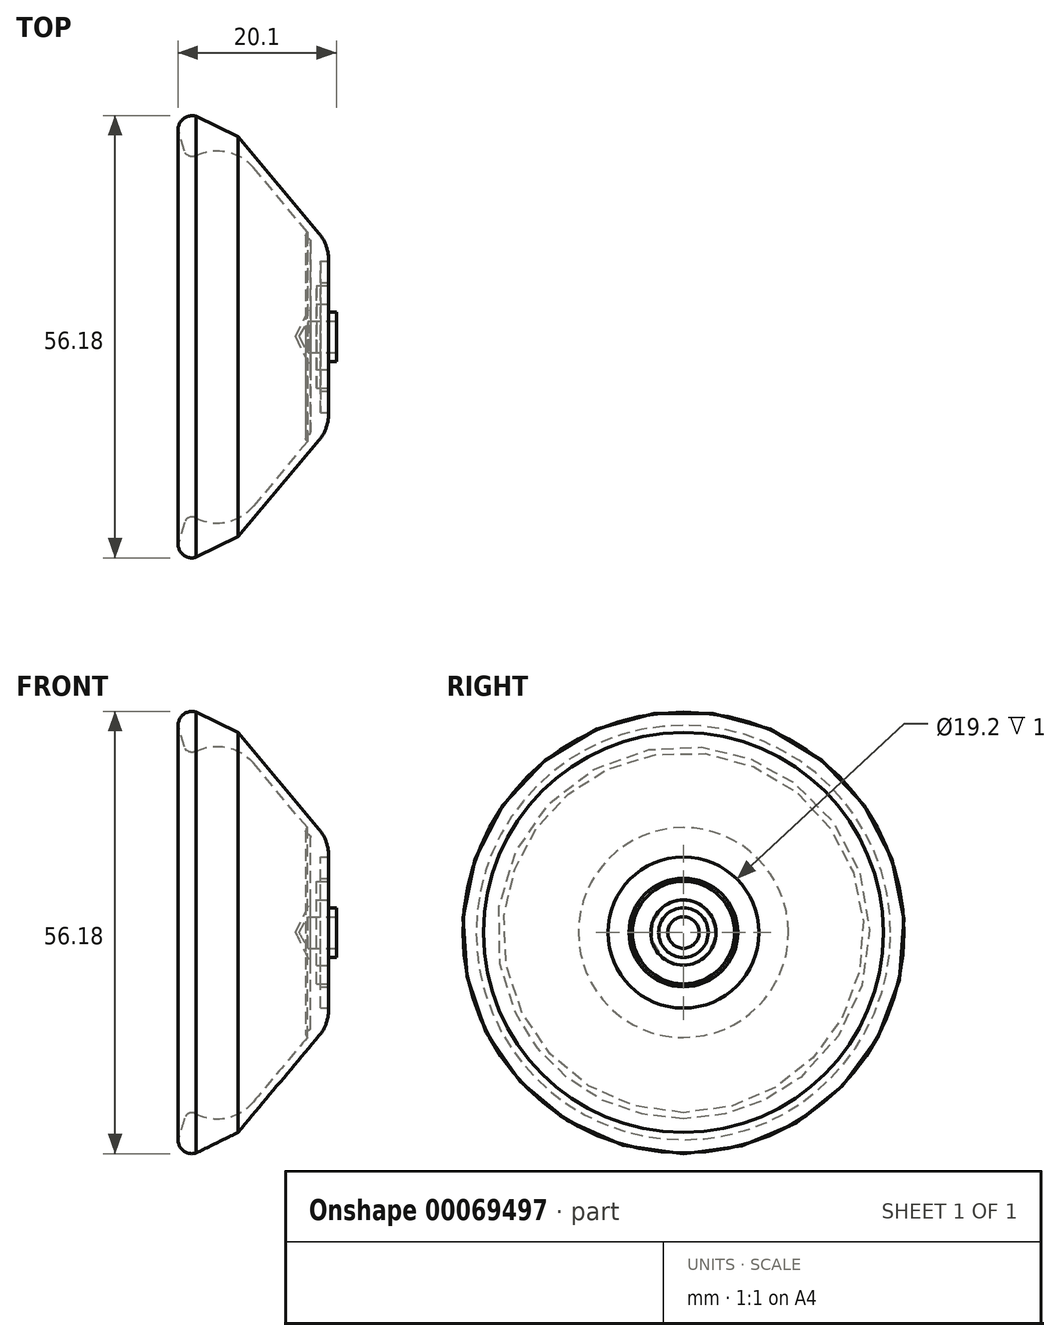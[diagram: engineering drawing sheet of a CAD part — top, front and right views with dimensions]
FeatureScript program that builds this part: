
annotation { "Feature Type Name" : "Feature", "Feature Type Description" : "" }
export const myFeature = defineFeature(function(context is Context, id is Id, definition is map)
    precondition{}
    {
        {
            var Q0;
            Q0=qCreatedBy(makeId("Front.planeOp"),FACE);
            var sketch = newSketch(context, id + "F0", { "sketchPlane" : qUnion([Q0])});
            skLineSegment(sketch, "E0", {"start": v(-1.4, 2) * mm, "end": v(-5, 2) * mm});
            skLineSegment(sketch, "E1", {"start": v(-5, 2) * mm, "end": v(-6.15, 0) * mm});
            skLineSegment(sketch, "E2", {"start": v(-6.15, 0) * mm, "end": v(-6.57, 0) * mm});
            skLineSegment(sketch, "E3", {"start": v(-5.08, 13.33) * mm, "end": v(-11.95, 21.51) * mm});
            skLineSegment(sketch, "E4", {"start": v(-1.4, 3.15) * mm, "end": v(-2.4, 3.15) * mm});
            skLineSegment(sketch, "E5", {"start": v(-2.4, 3.15) * mm, "end": v(-2.4, 4.15) * mm});
            skLineSegment(sketch, "E6", {"start": v(-2.4, 4.15) * mm, "end": v(-3.9, 4.15) * mm});
            skLineSegment(sketch, "E7", {"start": v(-3.9, 4.15) * mm, "end": v(-3.9, 6.5) * mm});
            skLineSegment(sketch, "E8", {"start": v(-3.9, 6.5) * mm, "end": v(-2.4, 6.5) * mm});
            skLineSegment(sketch, "E9", {"start": v(-2.4, 6.5) * mm, "end": v(-2.4, 6.9) * mm});
            skLineSegment(sketch, "E10", {"start": v(-2.4, 6.9) * mm, "end": v(-3.4, 6.9) * mm});
            skLineSegment(sketch, "E11", {"start": v(-3.4, 6.9) * mm, "end": v(-3.4, 9.6) * mm});
            skLineSegment(sketch, "E12", {"start": v(-3.4, 9.6) * mm, "end": v(-2.4, 9.6) * mm});
            skLineSegment(sketch, "E13", {"start": v(-2.4, 9.6) * mm, "end": v(-2.4, 9.87) * mm});
            skLineSegment(sketch, "E14", {"start": v(-1.4, 3.15) * mm, "end": v(-1.4, 2) * mm});
            skLineSegment(sketch, "E15", {"start": v(-13.9, 25.4) * mm, "end": v(-3.57, 13.09) * mm});
            skLineSegment(sketch, "E16", {"start": v(-4.65, 4) * mm, "end": v(-4.65, 12.1) * mm});
            skPoint(sketch, "E17.visualSharp", {"position": v(-2.4, 11.7) * mm});
            skArc(sketch, "E17.filletArc", {"start": v(-2.4, 9.87) * mm, "mid": v(-2.7, 11.58) * mm, "end": v(-3.57, 13.09) * mm});
            skLineSegment(sketch, "E18", {"start": v(-4.77, 12.34) * mm, "end": v(-5.12, 12.6) * mm});
            skLineSegment(sketch, "E19", {"start": v(-5.2, 13.16) * mm, "end": v(-5.08, 13.33) * mm});
            skPoint(sketch, "E20.visualSharp", {"position": v(-4.65, 12.25) * mm});
            skArc(sketch, "E20.filletArc", {"start": v(-4.65, 12.1) * mm, "mid": v(-4.68, 12.23) * mm, "end": v(-4.77, 12.34) * mm});
            skPoint(sketch, "E21.visualSharp", {"position": v(-5.44, 12.83) * mm});
            skArc(sketch, "E21.filletArc", {"start": v(-5.2, 13.16) * mm, "mid": v(-5.28, 12.86) * mm, "end": v(-5.12, 12.6) * mm});
            skLineSegment(sketch, "E22", {"start": v(-13.9, 25.4) * mm, "end": v(-19.2, 28) * mm});
            skArc(sketch, "E23", {"start": v(-19.2, 28) * mm, "mid": v(-20.78, 27.75) * mm, "end": v(-21.5, 26.32) * mm});
            skPoint(sketch, "E24.visualSharp", {"position": v(-15.03, 25.19) * mm});
            skArc(sketch, "E24.filletArc", {"start": v(-11.95, 21.51) * mm, "mid": v(-15.35, 23.54) * mm, "end": v(-19.27, 23) * mm});
            skLineSegment(sketch, "E25", {"start": v(-21.5, 26.32) * mm, "end": v(-20.68, 23.6) * mm});
            skPoint(sketch, "E26.visualSharp", {"position": v(-20.3, 22.33) * mm});
            skArc(sketch, "E26.filletArc", {"start": v(-20.68, 23.6) * mm, "mid": v(-20.12, 22.97) * mm, "end": v(-19.27, 23) * mm});
            skLineSegment(sketch, "E27", {"start": v(-6.57, 0) * mm, "end": v(-4.65, 4) * mm});
            skSolve(sketch);
        }
        {
            var Q0;
            Q0=qSketchRegion(id+"F0",true);
            var Q1;
            Q1=sQuery(id+"F0.wireOp",EDGE,"E2");
            revolve(context, id + "F1", {"entities" : qUnion([Q0]), "axis" : qUnion([Q1]), "revolveType" : RevolveType.FULL});
        }
    });
